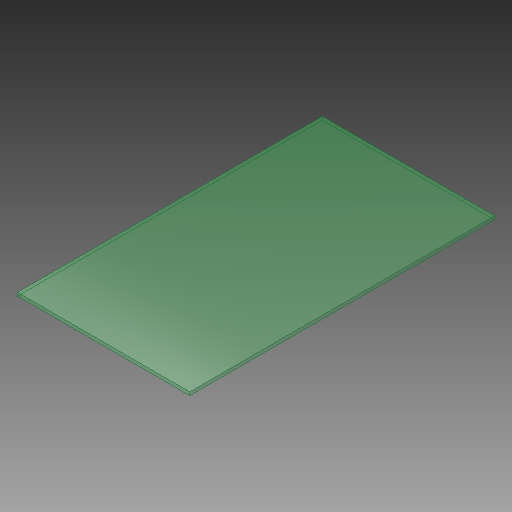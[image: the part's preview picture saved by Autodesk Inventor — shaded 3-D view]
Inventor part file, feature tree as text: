
AUTODESK INVENTOR PART (.ipt)
format: ipt  version: 2018.1 (Build 221171000, 171)  size: 101,376 bytes
history: native  units: mm
features: reference x4, other x4, extrude x2, sketch x2
ambient origin geometry x8: Origin, YZ Plane, XZ Plane, XY Plane, X Axis, Y Axis, Z Axis, Center Point
bodies: Solid1 (feature_tree)
feature tree (12):
  extrude  "Extrusion1"  Depth=460.0mm
  extrude  "Extrusion3"  TaperAngle=0.0deg  [1 undecoded]
  sketch  "Sketch1"  dims[d0=260.0mm d1=460.0mm]
  sketch  "Sketch3"  dims[d2=5.0mm d3=0.0mm d8=5.0mm d9=0.0mm]
  reference  "Reference1"
  reference  "Reference2"
  reference  "Reference3"
  reference  "Reference4"
  parser-record x1  (decoder bookkeeping rows leaked as tree rows — omitted from the tree; the rows remain in map.json)
  other  "eb_lid_assembly.iam"
  other  "tank_lid_handle_assembly:2"
  other  "tank_lid_handle_support:1"
note: 1 required parameter value undecoded (feature->parameter linkage not recoverable at this tier; creation-order binding heuristic only, values carry confidence <= 0.55)
note: 1 file-system path scrubbed to <path> (originals preserved in map.json)
